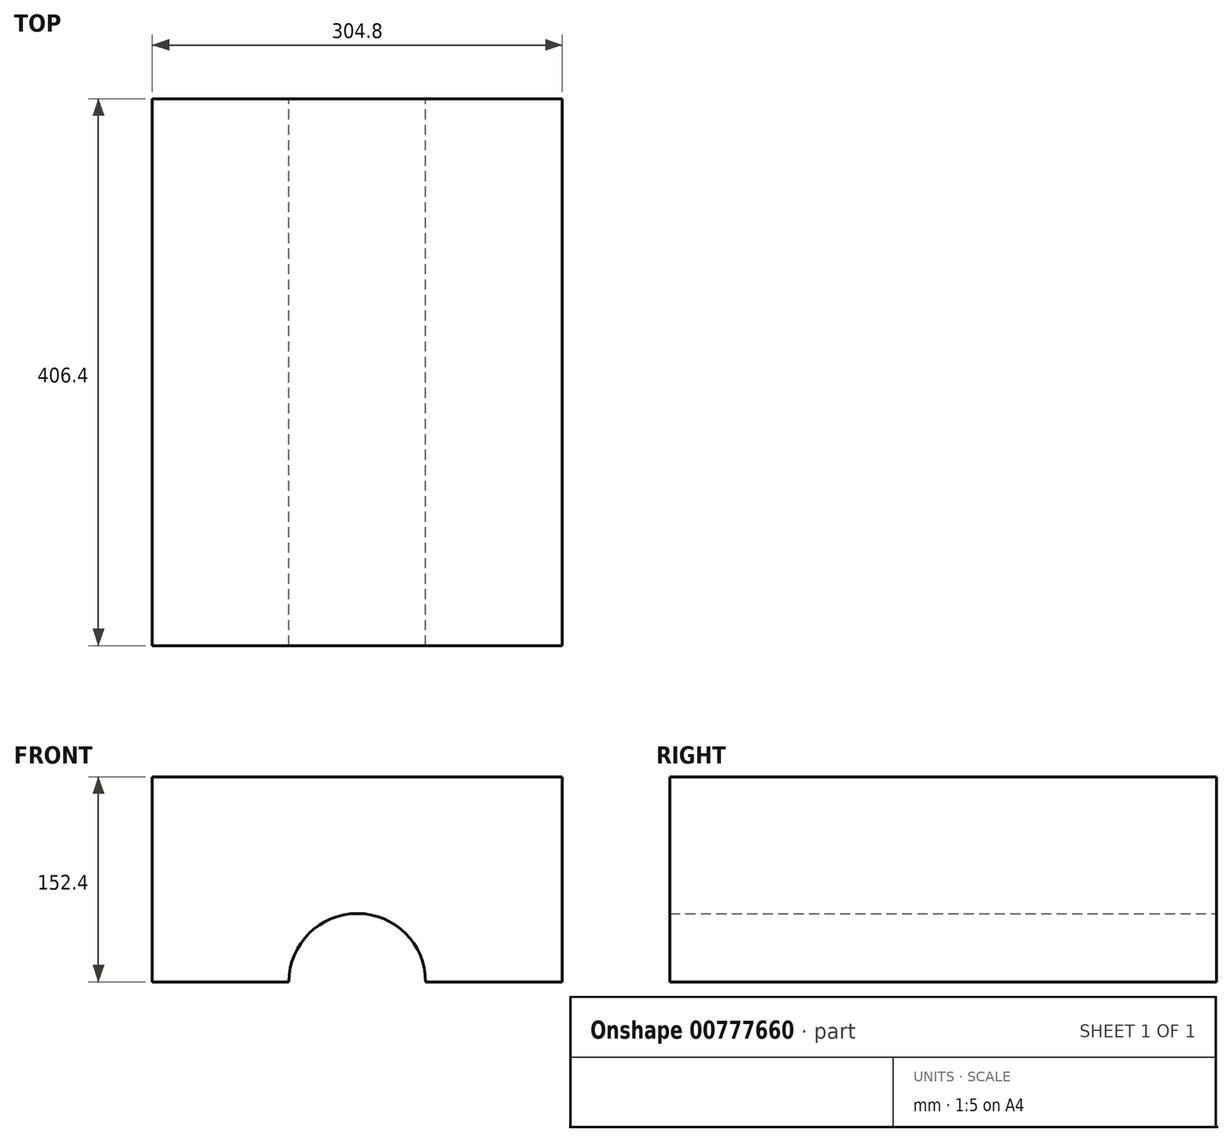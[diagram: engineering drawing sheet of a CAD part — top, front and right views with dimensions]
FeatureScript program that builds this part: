
annotation { "Feature Type Name" : "Feature", "Feature Type Description" : "" }
export const myFeature = defineFeature(function(context is Context, id is Id, definition is map)
    precondition{}
    {
        {
            var Q0;
            Q0=qCreatedBy(makeId("Front.planeOp"),FACE);
            var sketch = newSketch(context, id + "F0", { "sketchPlane" : qUnion([Q0])});
            skCircle(sketch, "E0", {"center": v(0, 0) * mm, "radius": 50.8 * mm});
            skLineSegment(sketch, "E1", {"start": v(-50.8, 0) * mm, "end": v(50.8, 0) * mm});
            skLineSegment(sketch, "E2.bottom", {"start": v(-19, 0) * mm, "end": v(19, 0) * mm});
            skLineSegment(sketch, "E2.top", {"start": v(-19, 47.11) * mm, "end": v(19, 47.11) * mm});
            skLineSegment(sketch, "E2.left", {"start": v(-19, 0) * mm, "end": v(-19, 47.11) * mm});
            skLineSegment(sketch, "E2.right", {"start": v(19, 0) * mm, "end": v(19, 47.11) * mm});
            skLineSegment(sketch, "E3.bottom", {"start": v(-152.4, 0) * mm, "end": v(152.4, 0) * mm});
            skLineSegment(sketch, "E3.top", {"start": v(-152.4, 152.4) * mm, "end": v(152.4, 152.4) * mm});
            skLineSegment(sketch, "E3.left", {"start": v(-152.4, 0) * mm, "end": v(-152.4, 152.4) * mm});
            skLineSegment(sketch, "E3.right", {"start": v(152.4, 0) * mm, "end": v(152.4, 152.4) * mm});
            skSolve(sketch);
        }
        {
            var Q0;
            Q0=makeQuery(id+"F0.imprint","IMPRINT",FACE,{"disambiguationData":[TD([[makeQuery(id+"F0.imprint","IMPRINT",EDGE,{"derivedFrom":sQuery(id+"F0.wireOp",EDGE,"E3.top")}),-1.0]])]});
            extrude(context, id + "F1", {"entities" : qUnion([Q0]), "depth" : 406.4 * mm, "offsetDistance" : 25.4 * mm});
        }
    });
